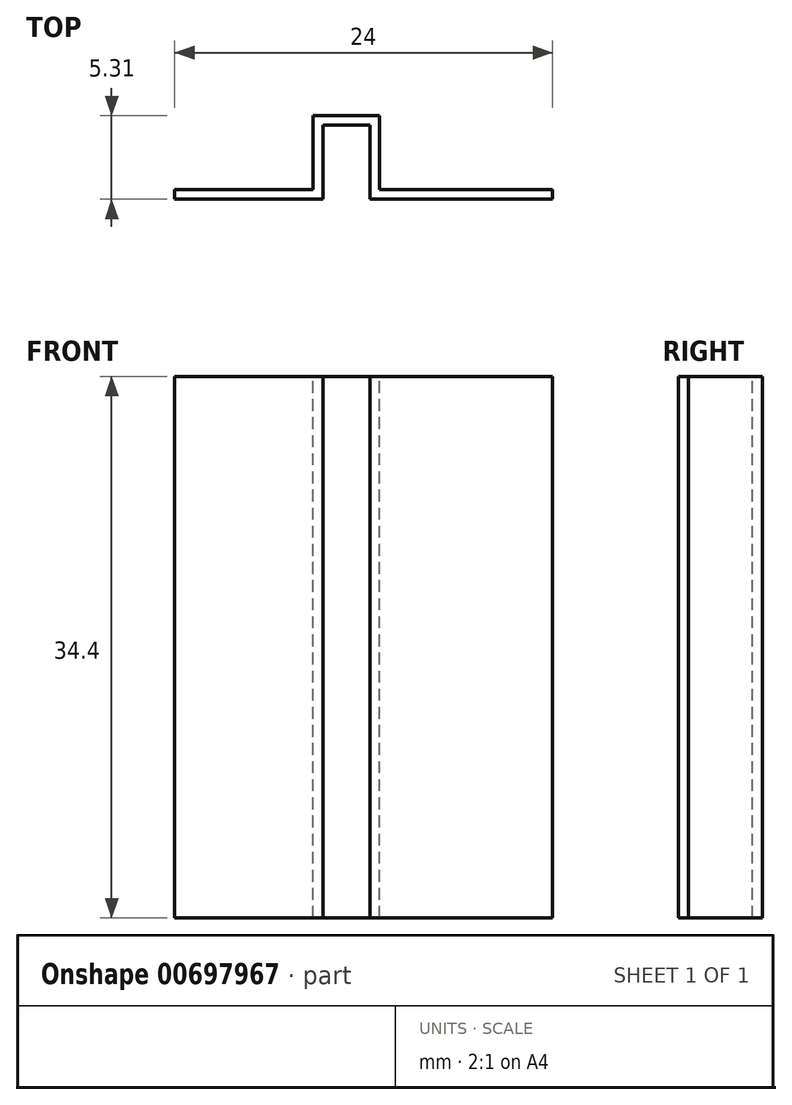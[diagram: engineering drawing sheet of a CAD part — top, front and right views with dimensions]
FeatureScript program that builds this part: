
annotation { "Feature Type Name" : "Feature", "Feature Type Description" : "" }
export const myFeature = defineFeature(function(context is Context, id is Id, definition is map)
    precondition{}
    {
        {
            var Q0;
            Q0=qCreatedBy(makeId("Front.planeOp"),FACE);
            var sketch = newSketch(context, id + "F0", { "sketchPlane" : qUnion([Q0])});
            skLineSegment(sketch, "E0.bottom", {"start": v(0, 0) * mm, "end": v(24, 0) * mm});
            skLineSegment(sketch, "E0.top", {"start": v(0, 34.4) * mm, "end": v(24, 34.4) * mm});
            skLineSegment(sketch, "E0.left", {"start": v(0, 0) * mm, "end": v(0, 34.4) * mm});
            skLineSegment(sketch, "E0.right", {"start": v(24, 0) * mm, "end": v(24, 34.4) * mm});
            skSolve(sketch);
        }
        {
            var Q0;
            Q0 = qSketchRegion(id + "F0", true);
            extrude(context, id + "F1", {"entities" : qUnion([Q0]), "depth" : 25 * mm, "offsetDistance" : 25 * mm});
        }
        {
            var Q0;
            Q0=makeQuery(id+"F1.opExtrude","CAP_FACE",FACE,{"disambiguationData":[OSD([sQuery(id+"F0.wireOp",EDGE,"E0.bottom"),sQuery(id+"F0.wireOp",EDGE,"E0.top"),sQuery(id+"F0.wireOp",EDGE,"E0.left"),sQuery(id+"F0.wireOp",EDGE,"E0.right")])],"isStart":false});
            var sketch = newSketch(context, id + "F2", { "sketchPlane" : qUnion([Q0])});
            skLineSegment(sketch, "E1.bottom", {"start": v(9.4, 0) * mm, "end": v(12.4, 0) * mm});
            skLineSegment(sketch, "E1.top", {"start": v(9.4, 34.4) * mm, "end": v(12.4, 34.4) * mm});
            skLineSegment(sketch, "E1.left", {"start": v(9.4, 0) * mm, "end": v(9.4, 34.4) * mm});
            skLineSegment(sketch, "E1.right", {"start": v(12.4, 0) * mm, "end": v(12.4, 34.4) * mm});
            skSolve(sketch);
        }
        {
            var Q0;
            Q0 = qSketchRegion(id + "F2", true);
            extrude(context, id + "F3", {"entities" : qUnion([Q0]), "operationType" : NewBodyOperationType.REMOVE, "oppositeDirection" : true, "depth" : 4.7 * mm, "offsetDistance" : 25 * mm});
        }
        {
            var Q0;
            Q0=makeQuery(id+"F1.opExtrude","CAP_FACE",FACE,{"disambiguationData":[OSD([sQuery(id+"F0.wireOp",EDGE,"E0.bottom"),sQuery(id+"F0.wireOp",EDGE,"E0.top"),sQuery(id+"F0.wireOp",EDGE,"E0.left"),sQuery(id+"F0.wireOp",EDGE,"E0.right")])],"isStart":true});
            var Q1;
            Q1=makeQuery(id+"F1.opExtrude","SWEPT_FACE",FACE,{"disambiguationData":[OSD([sQuery(id+"F0.wireOp",EDGE,"E0.left")])]});
            var Q2;
            Q2=makeQuery(id+"F1.opExtrude","SWEPT_FACE",FACE,{"disambiguationData":[OSD([sQuery(id+"F0.wireOp",EDGE,"E0.bottom")])]});
            var Q3;
            Q3=makeQuery(id+"F1.opExtrude","SWEPT_FACE",FACE,{"disambiguationData":[OSD([sQuery(id+"F0.wireOp",EDGE,"E0.right")])]});
            var Q4;
            Q4=makeQuery(id+"F1.opExtrude","SWEPT_FACE",FACE,{"disambiguationData":[OSD([sQuery(id+"F0.wireOp",EDGE,"E0.top")])]});
            shell(context, id + "F4", {"entities" : qUnion([Q0, Q1, Q2, Q3, Q4]), "thickness" : .61 * mm});
        }
    });
